# Revit family: Building-IEC309Connections-GEWISS-IEC309HP-10°_SURFACE-MOUNT_SOCKET_32A_IP67
name_source: partatom
category: Apparecchi elettrici
units: mm (PartAtom-declared; Revit-internal decimal feet)

## family parameters
Condiviso = No
Host = Superficie
Mantenere orientamento annotazione = Sì
Punto di calcolo locali = Sì
Quota connettore circolare = Usa diametro
Taglio con vuoti quando caricato = No
Tipo di parte = Normale

## types (12) — shared parameters
BLOCCO = B=C
Breaking capacity at 1.1 Un = 40A
Catalogue = BUILDING
Corpo centrale = Default(2)
Electrocod = 2211
FORMULA = 1000 mm  [stored 3.28084 ft]
Frequency = 50/60 Hz
Glow wire test: = 850 °C (active parts) - 650 °C (passive parts)
IDF = 70548aa2-ccde-4a04-a935-6f21e69494e9
IDT = a26e6f27ce1c4ce1acf7a3737c6fb816
IP degree = IP67
Immagine tipo = <Nessuno>
Insulation resistance = - 10 M?
L = 155 mm
Operating temperature: = -25 +55 °C
Permissible overload = 42A
Piastra = Default(2)
Produttore = GEWISS S.p.A.
Prospetto di default = 500 mm
Rated current (A) = 32
SEO = Socket outlet
SPinotto = Default(2)
Shock resistance = IK08
Sportello_visibile = Sì
Spostamento_S = 955 mm
Technical sheet = https://www.gewiss.com
Terminal tightening capacity = 2.5-6mm² flexible cables - 2.5-10mm² rigid cables
Thermo-pressure with ball = 125 °C (active parts) - 80 °C (passive parts)
Total number of operations = -2000
Type of wiring = With screw
Typology = 10° angled surface-mounting socket-outlet
URL = https://www.gewiss.com
Version file RFA = 21.11
W = 115 mm

## per-type parameters (varying)
| type | Colour: | Descrizione | Modello | No. of poles | Rated voltage | Reference h |
| GW62556 - IP67 10°W.RECEPTACLE 3P+E 32A 380V 3H | Red | IP67 10°W.RECEPTACLE 3P+E 32A 380V 3H | GW62556 | 3P+E | 380-440V | 3 |
| GW62441 - IP67 10°W.RECEPTACLE 3P+E 32A 400V 6H | Red | IP67 10°W.RECEPTACLE 3P+E 32A 400V 6H | GW62441 | 3P+E | 380-415V | 6 |
| GW62444 - IP67 10°W.RECEPTACLE 3P+N+T 32A 500V 7H | Black | IP67 10°W.RECEPTACLE 3P+N+T 32A 500V 7H | GW62444 | 3P+N+E | 480-500V | 7 |
| GW62436 - IP67 10°W.RECEPTACLE 3P+N+T 32A 110V 4H | Yellow | IP67 10°W.RECEPTACLE 3P+N+T 32A 110V 4H | GW62436 | 3P+N+E | 100-130V | 4 |
| GW62443 - IP67 10°W.RECEPTACLE 3P+E 32A 500V 7H | Black | IP67 10°W.RECEPTACLE 3P+E 32A 500V 7H | GW62443 | 3P+E | 480-500V | 7 |
| GW62434 - IP67 10°W.RECEPTACLE 2P+E 32A 110V 4H | Yellow | IP67 10°W.RECEPTACLE 2P+E 32A 110V 4H | GW62434 | 2P+E | 100-130V | 4 |
| GW62435 - IP67 10°W.RECEPTACLE 3P+E 32A 110V 4H | Yellow | IP67 10°W.RECEPTACLE 3P+E 32A 110V 4H | GW62435 | 3P+E | 100-130V | 4 |
| GW62442 - IP67 10°W.RECEPTACLE 3P+N+T 32A 400V 6H | Red | IP67 10°W.RECEPTACLE 3P+N+T 32A 400V 6H | GW62442 | 3P+N+E | 380-415V | 6 |
| GW62440 - IP67 10°W.RECEPTACLE 2P+E 32A 400V 9H | Red | IP67 10°W.RECEPTACLE 2P+E 32A 400V 9H | GW62440 | 2P+E | 380-415V | 9 |
| GW62439 - IP67 10°W.RECEPTACLE 3P+N+T 32A 230V 9H | Blue | IP67 10°W.RECEPTACLE 3P+N+T 32A 230V 9H | GW62439 | 3P+N+E | 200-250V | 9 |
| GW62437 - IP67 10°W.RECEPTACLE 2P+E 32A 230V 6H | Blue | IP67 10°W.RECEPTACLE 2P+E 32A 230V 6H | GW62437 | 2P+E | 200-250V | 6 |
| GW62438 - IP67 10°W.RECEPTACLE 3P+E 32A 230V 9H | Blue | IP67 10°W.RECEPTACLE 3P+E 32A 230V 9H | GW62438 | 3P+E | 200-250V | 9 |

note: [stored X ft] marks values corroborated as IEEE doubles in the binary element streams (Revit-internal decimal feet)

## geometry (parser evidence)
native form markers: Sweep x2
no freeform markers — native parametric forms only
